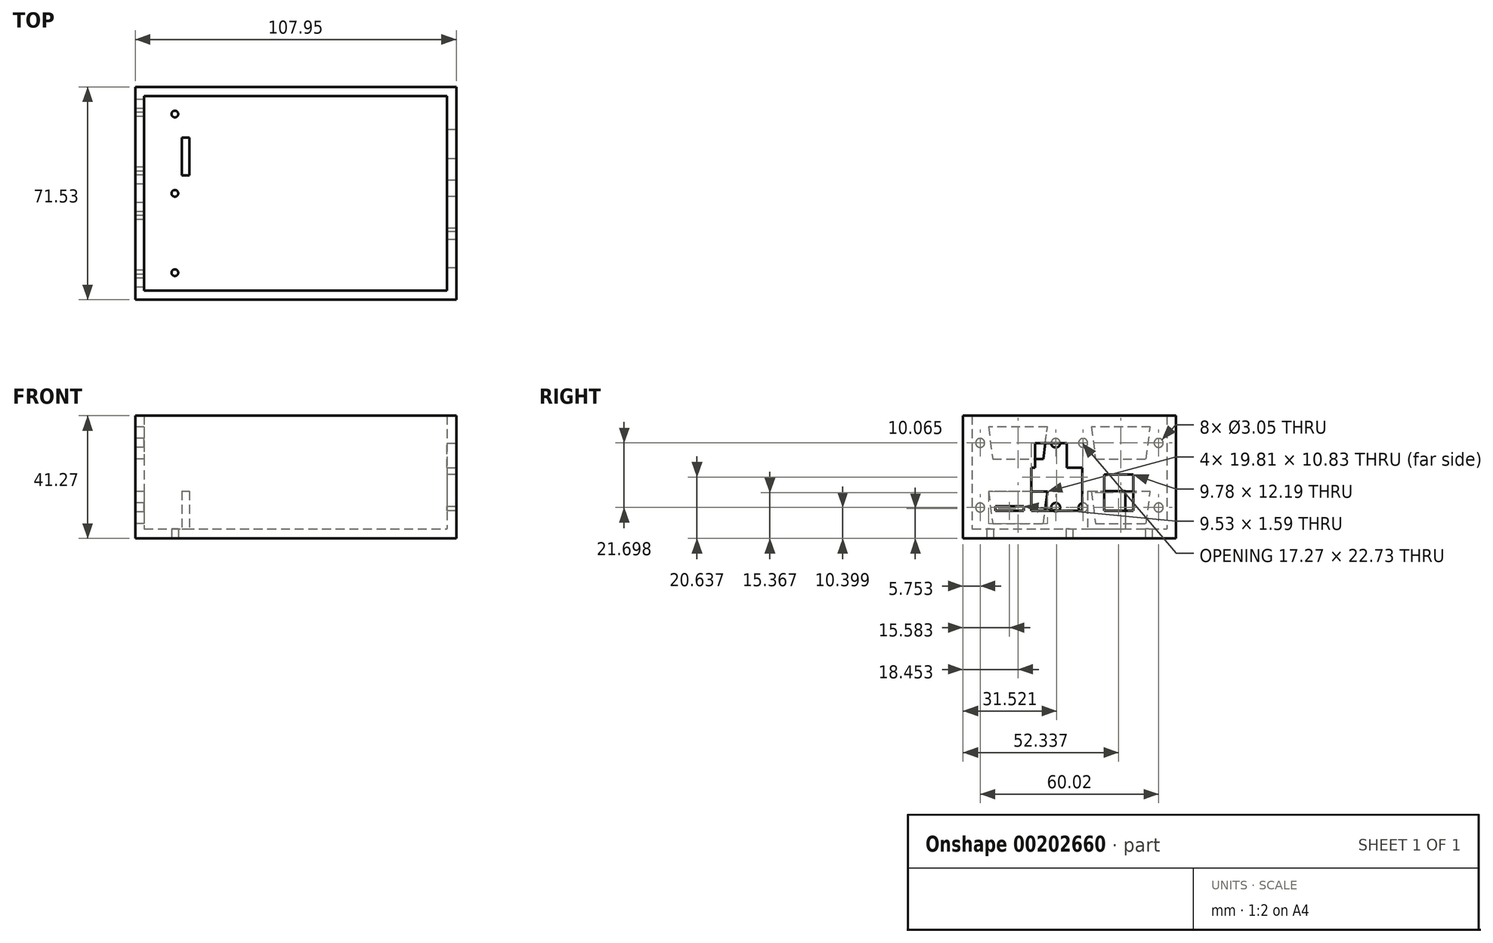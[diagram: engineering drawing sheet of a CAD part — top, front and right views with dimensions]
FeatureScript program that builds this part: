
annotation { "Feature Type Name" : "Feature", "Feature Type Description" : "" }
export const myFeature = defineFeature(function(context is Context, id is Id, definition is map)
    precondition{}
    {
        {
            var Q0;
            Q0=qCreatedBy(makeId("Top.planeOp"),FACE);
            var sketch = newSketch(context, id + "F0", { "sketchPlane" : qUnion([Q0])});
            skLineSegment(sketch, "E0.bottom", {"start": v(0, 71.53) * mm, "end": v(107.95, 71.53) * mm});
            skLineSegment(sketch, "E0.top", {"start": v(0, 0) * mm, "end": v(107.95, 0) * mm});
            skLineSegment(sketch, "E0.left", {"start": v(0, 71.53) * mm, "end": v(0, 0) * mm});
            skLineSegment(sketch, "E0.right", {"start": v(107.95, 71.53) * mm, "end": v(107.95, 0) * mm});
            skSolve(sketch);
        }
        {
            var Q0;
            Q0 = qSketchRegion(id + "F0", true);
            extrude(context, id + "F1", {"entities" : qUnion([Q0]), "depth" : 3.17 * mm});
        }
        {
            var Q0;
            Q0=makeQuery(id+"F1.opExtrude","CAP_FACE",FACE,{"disambiguationData":[OSD([sQuery(id+"F0.wireOp",EDGE,"E0.bottom"),sQuery(id+"F0.wireOp",EDGE,"E0.top"),sQuery(id+"F0.wireOp",EDGE,"E0.left"),sQuery(id+"F0.wireOp",EDGE,"E0.right")])],"isStart":false});
            var sketch = newSketch(context, id + "F2", { "sketchPlane" : qUnion([Q0])});
            skLineSegment(sketch, "E1", {"start": v(0, 71.53) * mm, "end": v(107.95, 71.53) * mm});
            skLineSegment(sketch, "E2", {"start": v(107.95, 71.53) * mm, "end": v(107.95, 0) * mm});
            skLineSegment(sketch, "E3", {"start": v(107.95, 0) * mm, "end": v(0, 0) * mm});
            skLineSegment(sketch, "E4", {"start": v(0, 0) * mm, "end": v(0, 3.03) * mm});
            skLineSegment(sketch, "E5", {"start": v(3.02, 3.03) * mm, "end": v(104.78, 3.03) * mm});
            skLineSegment(sketch, "E6", {"start": v(104.78, 3.03) * mm, "end": v(104.78, 68.5) * mm});
            skLineSegment(sketch, "E7", {"start": v(104.78, 68.5) * mm, "end": v(3.02, 68.5) * mm});
            skLineSegment(sketch, "E8", {"start": v(0, 68.5) * mm, "end": v(0, 71.53) * mm});
            skLineSegment(sketch, "E9", {"start": v(3.02, 68.5) * mm, "end": v(3.02, 3.03) * mm});
            skLineSegment(sketch, "E10", {"start": v(0, 68.5) * mm, "end": v(0, 3.03) * mm});
            skSolve(sketch);
        }
        {
            var Q0;
            Q0 = qSketchRegion(id + "F2", true);
            extrude(context, id + "F3", {"entities" : qUnion([Q0]), "operationType" : NewBodyOperationType.ADD, "depth" : 38.1 * mm});
        }
        {
            var Q0;
            {var subQ0=sQuery(id+"F2.wireOp",EDGE,"E6");Q0=makeQuery(id+"FK1xG3Yx18MsWMH_1.boolean.opBoolean","MERGE",FACE,{"derivedFrom":[makeQuery(id+"F3.opExtrude","SWEPT_FACE",FACE,{"disambiguationData":[OSD([subQ0])]}),makeQuery(id+"FK1xG3Yx18MsWMH_1.opExtrude","CAP_FACE",FACE,{"disambiguationData":[OSD([subQ0])],"isStart":false})]});}
            var sketch = newSketch(context, id + "F4", { "sketchPlane" : qUnion([Q0])});
            skLineSegment(sketch, "E11.bottom", {"start": v(-40.16, 23.75) * mm, "end": v(-22.89, 23.75) * mm});
            skLineSegment(sketch, "E11.top", {"start": v(-40.16, 9.27) * mm, "end": v(-22.89, 9.27) * mm});
            skLineSegment(sketch, "E11.left", {"start": v(-40.16, 23.75) * mm, "end": v(-40.16, 9.27) * mm});
            skLineSegment(sketch, "E11.right", {"start": v(-22.89, 23.75) * mm, "end": v(-22.89, 9.27) * mm});
            skLineSegment(sketch, "E12.bottom", {"start": v(-57.23, 21.46) * mm, "end": v(-47.45, 21.46) * mm});
            skLineSegment(sketch, "E12.top", {"start": v(-57.23, 9.27) * mm, "end": v(-47.45, 9.27) * mm});
            skLineSegment(sketch, "E12.left", {"start": v(-57.23, 21.46) * mm, "end": v(-57.23, 9.27) * mm});
            skLineSegment(sketch, "E12.right", {"start": v(-47.45, 21.46) * mm, "end": v(-47.45, 9.27) * mm});
            skLineSegment(sketch, "E13.bottom", {"start": v(-67.51, 31.18) * mm, "end": v(-4.01, 31.18) * mm, "construction": true});
            skLineSegment(sketch, "E13.top", {"start": v(-67.51, 28) * mm, "end": v(-4.01, 28) * mm, "construction": true});
            skLineSegment(sketch, "E13.left", {"start": v(-67.51, 31.18) * mm, "end": v(-67.51, 28) * mm, "construction": true});
            skLineSegment(sketch, "E13.right", {"start": v(-4.01, 31.18) * mm, "end": v(-4.01, 28) * mm, "construction": true});
            skLineSegment(sketch, "E14", {"start": v(-67.51, 29.6) * mm, "end": v(-68.5, 29.6) * mm, "construction": true});
            skLineSegment(sketch, "E15", {"start": v(-4.01, 29.45) * mm, "end": v(-3.03, 29.45) * mm, "construction": true});
            skSolve(sketch);
        }
        {
            var Q0;
            Q0 = qSketchRegion(id + "F4", true);
            extrude(context, id + "F5", {"entities" : qUnion([Q0]), "operationType" : NewBodyOperationType.REMOVE, "endBound" : BoundingType.THROUGH_ALL, "oppositeDirection" : true, "depth" : 25.4 * mm});
        }
        {
            var Q0;
            Q0=makeQuery(id+"F3.boolean.opBoolean","MERGE",FACE,{"derivedFrom":[makeQuery(id+"F1.opExtrude","SWEPT_FACE",FACE,{"disambiguationData":[OSD([sQuery(id+"F0.wireOp",EDGE,"E0.right")])]}),makeQuery(id+"F3.opExtrude","SWEPT_FACE",FACE,{"disambiguationData":[OSD([sQuery(id+"F2.wireOp",EDGE,"E2")])]})]});
            var sketch = newSketch(context, id + "F6", { "sketchPlane" : qUnion([Q0])});
            skLineSegment(sketch, "E16.bottom", {"start": v(10.82, 9.27) * mm, "end": v(20.35, 9.27) * mm});
            skLineSegment(sketch, "E16.top", {"start": v(10.82, 10.86) * mm, "end": v(20.35, 10.86) * mm});
            skLineSegment(sketch, "E16.left", {"start": v(10.82, 9.27) * mm, "end": v(10.82, 10.86) * mm});
            skLineSegment(sketch, "E16.right", {"start": v(20.35, 9.27) * mm, "end": v(20.35, 10.86) * mm});
            skSolve(sketch);
        }
        {
            var Q0;
            Q0 = qSketchRegion(id + "F6", true);
            extrude(context, id + "F7", {"entities" : qUnion([Q0]), "operationType" : NewBodyOperationType.REMOVE, "endBound" : BoundingType.UP_TO_NEXT, "oppositeDirection" : true, "depth" : 25.4 * mm});
        }
        {
            var Q0;
            Q0 = qSketchRegion(id + "F4", true);
            extrude(context, id + "F8", {"entities" : qUnion([Q0]), "operationType" : NewBodyOperationType.REMOVE, "endBound" : BoundingType.THROUGH_ALL, "oppositeDirection" : true, "depth" : 25.4 * mm});
        }
        {
            var Q0;
            Q0=makeQuery(id+"F1W6klfwgrSlYju_1.boolean.opBoolean","SPLIT",FACE,{"disambiguationData":[TD([makeQuery(id+"F3.opExtrude","SWEPT_FACE",FACE,{"disambiguationData":[OSD([sQuery(id+"F2.wireOp",EDGE,"E5")])]})])],"derivedFrom":makeQuery(id+"F1.opExtrude","CAP_FACE",FACE,{"disambiguationData":[OSD([sQuery(id+"F0.wireOp",EDGE,"E0.bottom"),sQuery(id+"F0.wireOp",EDGE,"E0.top"),sQuery(id+"F0.wireOp",EDGE,"E0.left"),sQuery(id+"F0.wireOp",EDGE,"E0.right")])],"isStart":false})});
            var sketch = newSketch(context, id + "F9", { "sketchPlane" : qUnion([Q0])});
            skLineSegment(sketch, "E17.bottom", {"start": v(15.7, 41.82) * mm, "end": v(18.24, 41.82) * mm});
            skLineSegment(sketch, "E17.top", {"start": v(15.7, 54.52) * mm, "end": v(18.24, 54.52) * mm});
            skLineSegment(sketch, "E17.left", {"start": v(15.7, 41.82) * mm, "end": v(15.7, 54.52) * mm});
            skLineSegment(sketch, "E17.right", {"start": v(18.24, 41.82) * mm, "end": v(18.24, 54.52) * mm});
            skSolve(sketch);
        }
        {
            var Q0;
            Q0 = qSketchRegion(id + "F9", true);
            extrude(context, id + "F10", {"entities" : qUnion([Q0]), "operationType" : NewBodyOperationType.ADD, "depth" : 12.7 * mm});
        }
        {
            var Q0;
            Q0=makeQuery(id+"F3.boolean.opBoolean","MERGE",FACE,{"derivedFrom":[makeQuery(id+"F1.opExtrude","SWEPT_FACE",FACE,{"disambiguationData":[OSD([sQuery(id+"F0.wireOp",EDGE,"E0.left")])]}),makeQuery(id+"F3.opExtrude","SWEPT_FACE",FACE,{"disambiguationData":[OSD([sQuery(id+"F2.wireOp",EDGE,"E4"),sQuery(id+"F2.wireOp",EDGE,"E8"),sQuery(id+"F2.wireOp",EDGE,"E10")])]})]});
            var sketch = newSketch(context, id + "F11", { "sketchPlane" : qUnion([Q0])});
            skLineSegment(sketch, "E18", {"start": v(-62.98, 37.51) * mm, "end": v(-43.17, 37.51) * mm});
            skLineSegment(sketch, "E19", {"start": v(-43.17, 37.51) * mm, "end": v(-44.56, 26.68) * mm});
            skLineSegment(sketch, "E20", {"start": v(-44.56, 26.68) * mm, "end": v(-61.58, 26.68) * mm});
            skLineSegment(sketch, "E21", {"start": v(-61.58, 26.68) * mm, "end": v(-62.98, 37.51) * mm});
            skLineSegment(sketch, "E22", {"start": v(-68.48, 38.38) * mm, "end": v(-37.67, 38.38) * mm, "construction": true});
            skLineSegment(sketch, "E23", {"start": v(-37.67, 38.38) * mm, "end": v(-37.67, 25.81) * mm, "construction": true});
            skLineSegment(sketch, "E24", {"start": v(-37.67, 25.81) * mm, "end": v(-68.48, 25.81) * mm, "construction": true});
            skLineSegment(sketch, "E25", {"start": v(-68.48, 25.81) * mm, "end": v(-68.48, 38.38) * mm, "construction": true});
            skLineSegment(sketch, "E26", {"start": v(-53.07, 37.51) * mm, "end": v(-53.07, 26.68) * mm, "construction": true});
            skLineSegment(sketch, "E27", {"start": v(-53.07, 32.1) * mm, "end": v(-37.67, 32.1) * mm, "construction": true});
            skLineSegment(sketch, "E28", {"start": v(-53.07, 32.1) * mm, "end": v(-68.48, 32.1) * mm, "construction": true});
            skLineSegment(sketch, "E29", {"start": v(-62.98, 15.82) * mm, "end": v(-43.17, 15.82) * mm});
            skLineSegment(sketch, "E30", {"start": v(-43.17, 15.82) * mm, "end": v(-44.56, 4.98) * mm});
            skLineSegment(sketch, "E31", {"start": v(-44.56, 4.98) * mm, "end": v(-61.58, 4.98) * mm});
            skLineSegment(sketch, "E32", {"start": v(-61.58, 4.98) * mm, "end": v(-62.98, 15.82) * mm});
            skLineSegment(sketch, "E33", {"start": v(-68.48, 16.69) * mm, "end": v(-37.67, 16.69) * mm, "construction": true});
            skLineSegment(sketch, "E34", {"start": v(-37.67, 16.69) * mm, "end": v(-37.67, 4.11) * mm, "construction": true});
            skLineSegment(sketch, "E35", {"start": v(-37.67, 4.11) * mm, "end": v(-68.48, 4.11) * mm, "construction": true});
            skLineSegment(sketch, "E36", {"start": v(-68.48, 4.11) * mm, "end": v(-68.48, 16.69) * mm, "construction": true});
            skLineSegment(sketch, "E37", {"start": v(-53.07, 15.82) * mm, "end": v(-53.07, 4.98) * mm, "construction": true});
            skLineSegment(sketch, "E38", {"start": v(-53.07, 10.4) * mm, "end": v(-37.67, 10.4) * mm, "construction": true});
            skLineSegment(sketch, "E39", {"start": v(-53.07, 10.4) * mm, "end": v(-68.48, 10.4) * mm, "construction": true});
            skLineSegment(sketch, "E40", {"start": v(-28.36, 37.51) * mm, "end": v(-8.55, 37.51) * mm});
            skLineSegment(sketch, "E41", {"start": v(-8.55, 37.51) * mm, "end": v(-9.94, 26.68) * mm});
            skLineSegment(sketch, "E42", {"start": v(-9.94, 26.68) * mm, "end": v(-26.96, 26.68) * mm});
            skLineSegment(sketch, "E43", {"start": v(-26.96, 26.68) * mm, "end": v(-28.36, 37.51) * mm});
            skLineSegment(sketch, "E44", {"start": v(-33.86, 38.38) * mm, "end": v(-3.05, 38.38) * mm, "construction": true});
            skLineSegment(sketch, "E45", {"start": v(-3.05, 38.38) * mm, "end": v(-3.05, 25.81) * mm, "construction": true});
            skLineSegment(sketch, "E46", {"start": v(-3.05, 25.81) * mm, "end": v(-33.86, 25.81) * mm, "construction": true});
            skLineSegment(sketch, "E47", {"start": v(-33.86, 25.81) * mm, "end": v(-33.86, 38.38) * mm, "construction": true});
            skLineSegment(sketch, "E48", {"start": v(-18.45, 37.51) * mm, "end": v(-18.45, 26.68) * mm, "construction": true});
            skLineSegment(sketch, "E49", {"start": v(-18.45, 32.1) * mm, "end": v(-3.05, 32.1) * mm, "construction": true});
            skLineSegment(sketch, "E50", {"start": v(-18.45, 32.1) * mm, "end": v(-33.86, 32.1) * mm, "construction": true});
            skLineSegment(sketch, "E51", {"start": v(-28.36, 15.82) * mm, "end": v(-8.55, 15.82) * mm});
            skLineSegment(sketch, "E52", {"start": v(-8.55, 15.82) * mm, "end": v(-9.94, 4.98) * mm});
            skLineSegment(sketch, "E53", {"start": v(-9.94, 4.98) * mm, "end": v(-26.96, 4.98) * mm});
            skLineSegment(sketch, "E54", {"start": v(-26.96, 4.98) * mm, "end": v(-28.36, 15.82) * mm});
            skLineSegment(sketch, "E55", {"start": v(-33.86, 16.69) * mm, "end": v(-3.05, 16.69) * mm, "construction": true});
            skLineSegment(sketch, "E56", {"start": v(-3.05, 16.69) * mm, "end": v(-3.05, 4.11) * mm, "construction": true});
            skLineSegment(sketch, "E57", {"start": v(-3.05, 4.11) * mm, "end": v(-33.86, 4.11) * mm, "construction": true});
            skLineSegment(sketch, "E58", {"start": v(-33.86, 4.11) * mm, "end": v(-33.86, 16.69) * mm, "construction": true});
            skLineSegment(sketch, "E59", {"start": v(-18.45, 15.82) * mm, "end": v(-18.45, 4.98) * mm, "construction": true});
            skLineSegment(sketch, "E60", {"start": v(-18.45, 10.4) * mm, "end": v(-3.05, 10.4) * mm, "construction": true});
            skLineSegment(sketch, "E61", {"start": v(-18.45, 10.4) * mm, "end": v(-33.86, 10.4) * mm, "construction": true});
            skCircle(sketch, "E62", {"center": v(-40.37, 32.1) * mm, "radius": 1.52 * mm});
            skCircle(sketch, "E63", {"center": v(-65.77, 32.1) * mm, "radius": 1.52 * mm});
            skCircle(sketch, "E64", {"center": v(-65.77, 10.4) * mm, "radius": 1.52 * mm});
            skCircle(sketch, "E65", {"center": v(-40.37, 10.4) * mm, "radius": 1.52 * mm});
            skCircle(sketch, "E66", {"center": v(-31.15, 10.4) * mm, "radius": 1.52 * mm});
            skCircle(sketch, "E67", {"center": v(-5.75, 10.4) * mm, "radius": 1.52 * mm});
            skCircle(sketch, "E68", {"center": v(-5.75, 32.1) * mm, "radius": 1.52 * mm});
            skCircle(sketch, "E69", {"center": v(-31.15, 32.1) * mm, "radius": 1.52 * mm});
            skLineSegment(sketch, "E70", {"start": v(-71.53, 41.27) * mm, "end": v(0, 41.27) * mm, "construction": true});
            skLineSegment(sketch, "E71", {"start": v(-40.37, 32.1) * mm, "end": v(-31.15, 32.1) * mm, "construction": true});
            skLineSegment(sketch, "E72", {"start": v(-35.76, 32.1) * mm, "end": v(-35.76, 41.27) * mm, "construction": true});
            skSolve(sketch);
        }
        {
            var Q0;
            Q0 = qSketchRegion(id + "F11", true);
            extrude(context, id + "F12", {"entities" : qUnion([Q0]), "operationType" : NewBodyOperationType.REMOVE, "endBound" : BoundingType.UP_TO_NEXT, "oppositeDirection" : true, "depth" : 25.4 * mm});
        }
        {
            var Q0;
            Q0=makeQuery(id+"F1.opExtrude","CAP_FACE",FACE,{"disambiguationData":[OSD([sQuery(id+"F0.wireOp",EDGE,"E0.bottom"),sQuery(id+"F0.wireOp",EDGE,"E0.top"),sQuery(id+"F0.wireOp",EDGE,"E0.left"),sQuery(id+"F0.wireOp",EDGE,"E0.right")])],"isStart":true});
            var sketch = newSketch(context, id + "F13", { "sketchPlane" : qUnion([Q0])});
            skCircle(sketch, "E73", {"center": v(13.34, -62.43) * mm, "radius": 1.14 * mm});
            skCircle(sketch, "E74", {"center": v(13.33, -35.76) * mm, "radius": 1.14 * mm});
            skCircle(sketch, "E75", {"center": v(13.33, -9.1) * mm, "radius": 1.14 * mm});
            skLineSegment(sketch, "E76", {"start": v(0, -71.53) * mm, "end": v(0, 0) * mm, "construction": true});
            skLineSegment(sketch, "E77", {"start": v(13.33, -35.76) * mm, "end": v(0, -35.76) * mm, "construction": true});
            skSolve(sketch);
        }
        {
            var Q0;
            Q0 = qSketchRegion(id + "F13", true);
            extrude(context, id + "F14", {"entities" : qUnion([Q0]), "operationType" : NewBodyOperationType.REMOVE, "endBound" : BoundingType.THROUGH_ALL, "oppositeDirection" : true, "depth" : 25.4 * mm});
        }
        {
            var Q0;
            Q0=makeQuery(id+"F3.boolean.opBoolean","MERGE",FACE,{"derivedFrom":[makeQuery(id+"F1.opExtrude","SWEPT_FACE",FACE,{"disambiguationData":[OSD([sQuery(id+"F0.wireOp",EDGE,"E0.right")])]}),makeQuery(id+"F3.opExtrude","SWEPT_FACE",FACE,{"disambiguationData":[OSD([sQuery(id+"F2.wireOp",EDGE,"E2")])]})]});
            var sketch = newSketch(context, id + "F15", { "sketchPlane" : qUnion([Q0])});
            skLineSegment(sketch, "E78", {"start": v(34.82, 23.75) * mm, "end": v(34.82, 32) * mm});
            skLineSegment(sketch, "E79", {"start": v(34.82, 32) * mm, "end": v(24.16, 32) * mm});
            skLineSegment(sketch, "E80", {"start": v(24.16, 32) * mm, "end": v(24.16, 23.75) * mm});
            skLineSegment(sketch, "E81", {"start": v(24.16, 23.75) * mm, "end": v(34.82, 23.75) * mm});
            skSolve(sketch);
        }
        {
            var Q0;
            Q0 = qSketchRegion(id + "F15", true);
            extrude(context, id + "F16", {"entities" : qUnion([Q0]), "operationType" : NewBodyOperationType.REMOVE, "endBound" : BoundingType.UP_TO_NEXT, "oppositeDirection" : true, "depth" : 25.4 * mm});
        }
    });
